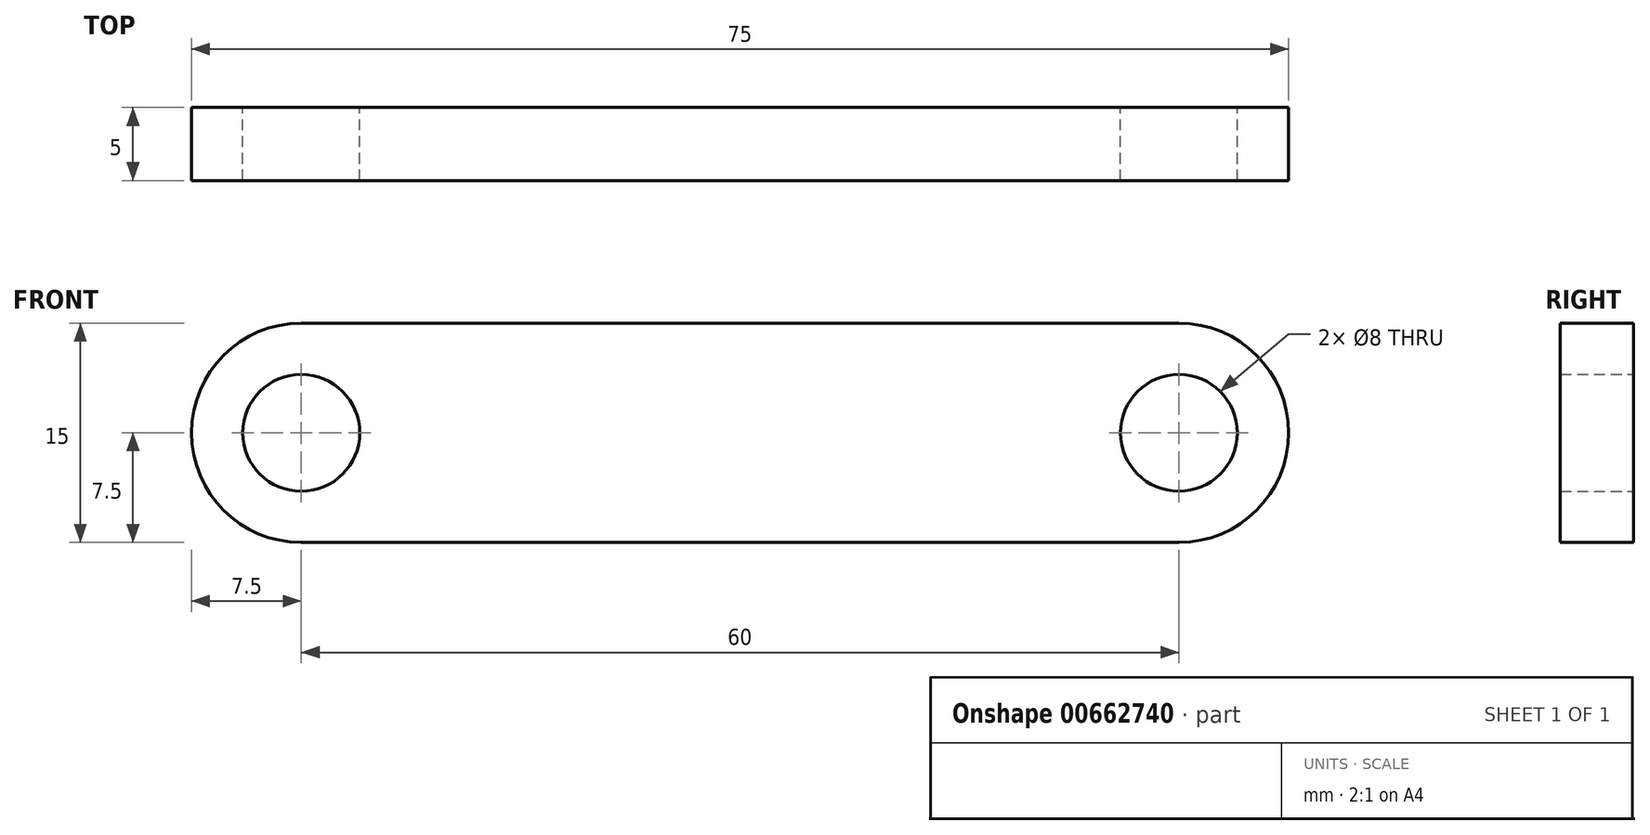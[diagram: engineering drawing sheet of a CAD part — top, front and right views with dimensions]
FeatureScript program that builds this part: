
annotation { "Feature Type Name" : "Feature", "Feature Type Description" : "" }
export const myFeature = defineFeature(function(context is Context, id is Id, definition is map)
    precondition{}
    {
        {
            var Q0;
            Q0=qCreatedBy(makeId("Front.planeOp"),FACE);
            var sketch = newSketch(context, id + "F0", { "sketchPlane" : qUnion([Q0])});
            skArc(sketch, "E0", {"start": v(0, 7.5) * mm, "mid": v(-7.5, 0) * mm, "end": v(0, -7.5) * mm});
            skArc(sketch, "E1", {"start": v(60, -7.5) * mm, "mid": v(67.5, 0) * mm, "end": v(60, 7.5) * mm});
            skLineSegment(sketch, "E2", {"start": v(0, 7.5) * mm, "end": v(60, 7.5) * mm});
            skLineSegment(sketch, "E3", {"start": v(0, -7.5) * mm, "end": v(60, -7.5) * mm});
            skCircle(sketch, "E4", {"center": v(0, 0) * mm, "radius": 4 * mm});
            skCircle(sketch, "E5", {"center": v(60, 0) * mm, "radius": 4 * mm});
            skSolve(sketch);
        }
        {
            var Q0;
            Q0 = qSketchRegion(id + "F0", true);
            extrude(context, id + "F1", {"entities" : qUnion([Q0]), "depth" : 5 * mm, "offsetDistance" : 25 * mm});
        }
    });
